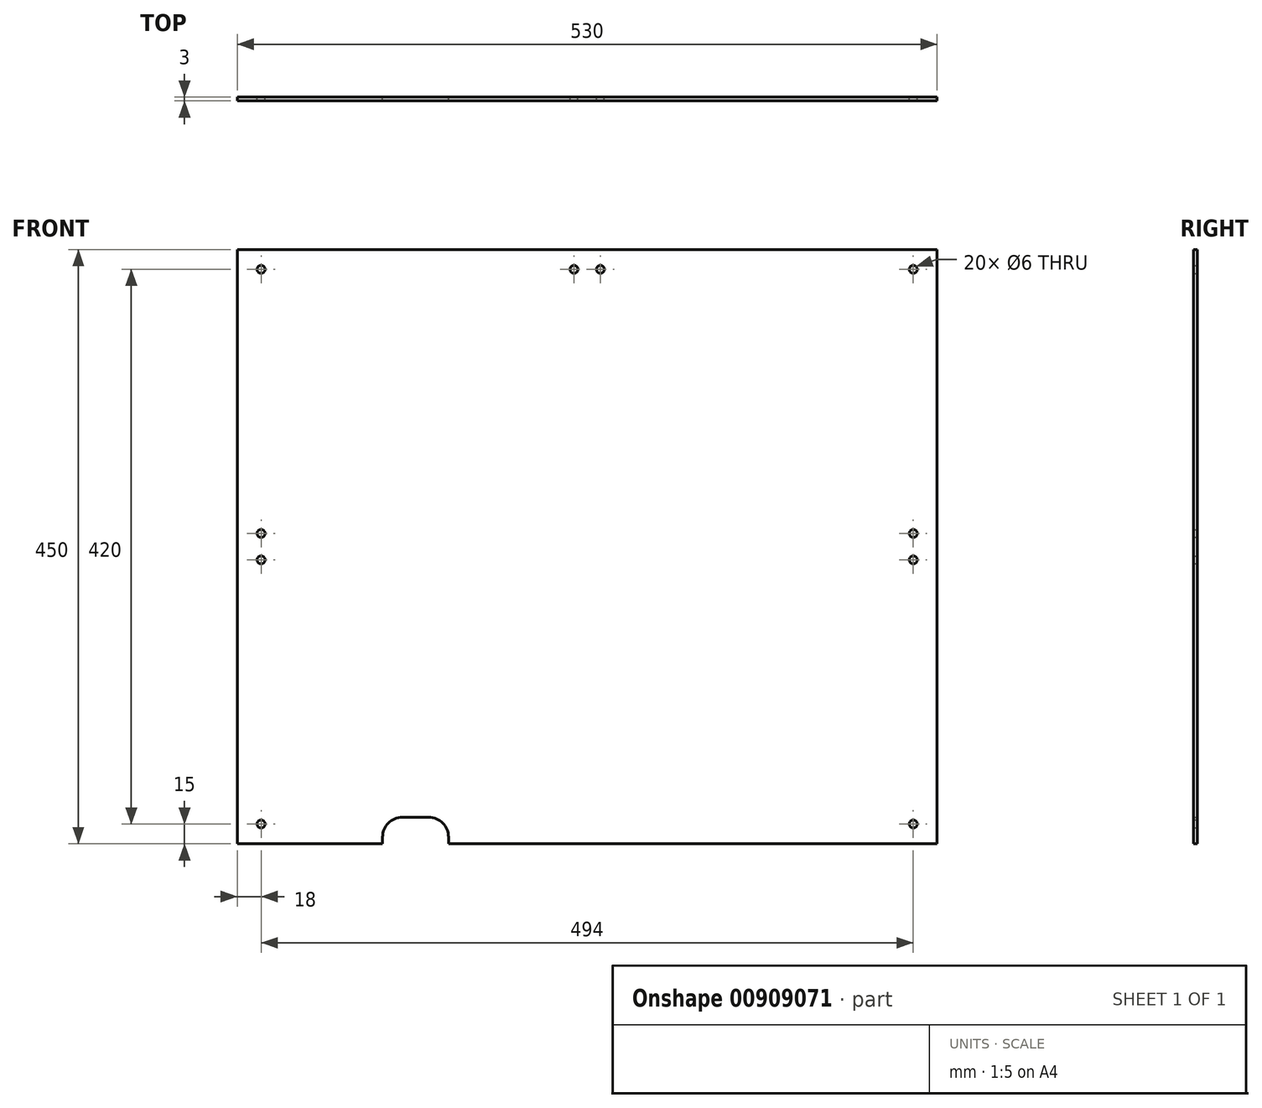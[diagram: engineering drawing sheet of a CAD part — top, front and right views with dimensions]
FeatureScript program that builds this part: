
annotation { "Feature Type Name" : "Feature", "Feature Type Description" : "" }
export const myFeature = defineFeature(function(context is Context, id is Id, definition is map)
    precondition{}
    {
        {
            var Q0;
            Q0=qCreatedBy(makeId("Front.planeOp"),FACE);
            var sketch = newSketch(context, id + "F0", { "sketchPlane" : qUnion([Q0])});
            skLineSegment(sketch, "E0.bottom", {"start": v(0, 0) * mm, "end": v(530, 0) * mm});
            skLineSegment(sketch, "E0.top", {"start": v(0, 450) * mm, "end": v(530, 450) * mm});
            skLineSegment(sketch, "E0.left", {"start": v(0, 0) * mm, "end": v(0, 450) * mm});
            skLineSegment(sketch, "E0.right", {"start": v(530, 0) * mm, "end": v(530, 450) * mm});
            skCircle(sketch, "E1", {"center": v(18, 15) * mm, "radius": 3 * mm});
            skCircle(sketch, "E2", {"center": v(512, 15) * mm, "radius": 3 * mm});
            skCircle(sketch, "E3", {"center": v(18, 435) * mm, "radius": 3 * mm});
            skCircle(sketch, "E4", {"center": v(512, 435) * mm, "radius": 3 * mm});
            skLineSegment(sketch, "E5.bottom", {"start": v(110, 0) * mm, "end": v(160, 0) * mm});
            skLineSegment(sketch, "E5.top", {"start": v(125, 20) * mm, "end": v(145, 20) * mm});
            skLineSegment(sketch, "E5.left", {"start": v(110, 0) * mm, "end": v(110, 5) * mm});
            skLineSegment(sketch, "E5.right", {"start": v(160, 0) * mm, "end": v(160, 5) * mm});
            skPoint(sketch, "E6.visualSharp", {"position": v(110, 20) * mm});
            skArc(sketch, "E6.filletArc", {"start": v(125, 20) * mm, "mid": v(114.4, 15.6) * mm, "end": v(110, 5) * mm});
            skPoint(sketch, "E7.visualSharp", {"position": v(160, 20) * mm});
            skArc(sketch, "E7.filletArc", {"start": v(160, 5) * mm, "mid": v(155.6, 15.6) * mm, "end": v(145, 20) * mm});
            skCircle(sketch, "E8", {"center": v(18, 235) * mm, "radius": 3 * mm});
            skCircle(sketch, "E9", {"center": v(18, 215) * mm, "radius": 3 * mm});
            skCircle(sketch, "E10", {"center": v(512, 235) * mm, "radius": 3 * mm});
            skCircle(sketch, "E11", {"center": v(512, 215) * mm, "radius": 3 * mm});
            skCircle(sketch, "E12", {"center": v(255, 435) * mm, "radius": 3 * mm});
            skCircle(sketch, "E13", {"center": v(275, 435) * mm, "radius": 3 * mm});
            skSolve(sketch);
        }
        {
            var Q0;
            Q0=makeQuery(id+"F0.imprint","IMPRINT",FACE,{"disambiguationData":[TD([[makeQuery(id+"F0.imprint","IMPRINT",EDGE,{"derivedFrom":sQuery(id+"F0.wireOp",EDGE,"E0.bottom")}),1.0]])]});
            extrude(context, id + "F1", {"entities" : qUnion([Q0]), "depth" : 3 * mm, "offsetDistance" : 25 * mm});
        }
    });
